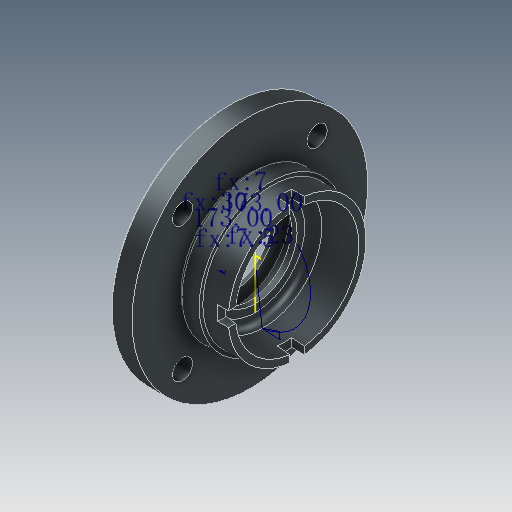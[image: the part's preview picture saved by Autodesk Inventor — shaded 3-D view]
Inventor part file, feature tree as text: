
AUTODESK INVENTOR PART (.ipt)
format: ipt  version: 2025 (Build 290162000, 162)  size: 254,464 bytes
history: native  units: in
note: dims shown in document units (in); Inventor stores cm internally (conversion verified against a paired STEP export)
features: sketch x6, extrude x3, revolve x2, chamfer x1, fillet x1
ambient origin geometry x8: Origin, YZ Plane, XZ Plane, XY Plane, X Axis, Y Axis, Z Axis, Center Point
bodies: 实体1 (feature_tree)
feature tree (13):
  revolve  "旋转1"  [1 undecoded]
  extrude  "拉伸1"  Depth=2.5591in
  extrude  "拉伸2"  Depth=0.4724in
  extrude  "拉伸3"  Depth=1.4961in
  chamfer  "倒角1"  Distance=1.4961in
  fillet  "圆角1"  [1 undecoded]
  sketch  "草图5"  dims[d9=0.0984in d10=1.4961in d11=45.0deg d12=0.0394in d13=0.5906in d14=1.3386in d15=0.5792in d16=90.0deg d17=0.2756in d18=0.315in d19=0.0in d20=0.2756in d21=0.315in d22=0.0in d23=0.4331in d24=2.0669in d25=1.5748in d27=360.0deg d29=0.315in d30=0.0in d31=0.0394in d32=0.0787in d33=45.0deg d34=0.1969in d35=0.9055in d36=1.1811in d37=0.2756in d38=0.0481in d39=0.0481in d40=0.2953in d41=90.0deg d42=45.0deg]
  revolve  "旋转2"  [1 undecoded]
  sketch  "草图1"  dims[d3=0.3937in d0=0.4331in]
  sketch  "草图2"  dims[d4=1.0236in d5=0.4724in]
  sketch  "草图3"  dims[d6=1.5748in d7=1.4961in]
  sketch  "草图4"  dims[d8=0.4724in]
  sketch  "草图 - 环形阵列1"  dims[d1=1.811in d2=2.5591in]
note: 3 required parameter values undecoded (feature->parameter linkage not recoverable at this tier; creation-order binding heuristic only, values carry confidence <= 0.55)